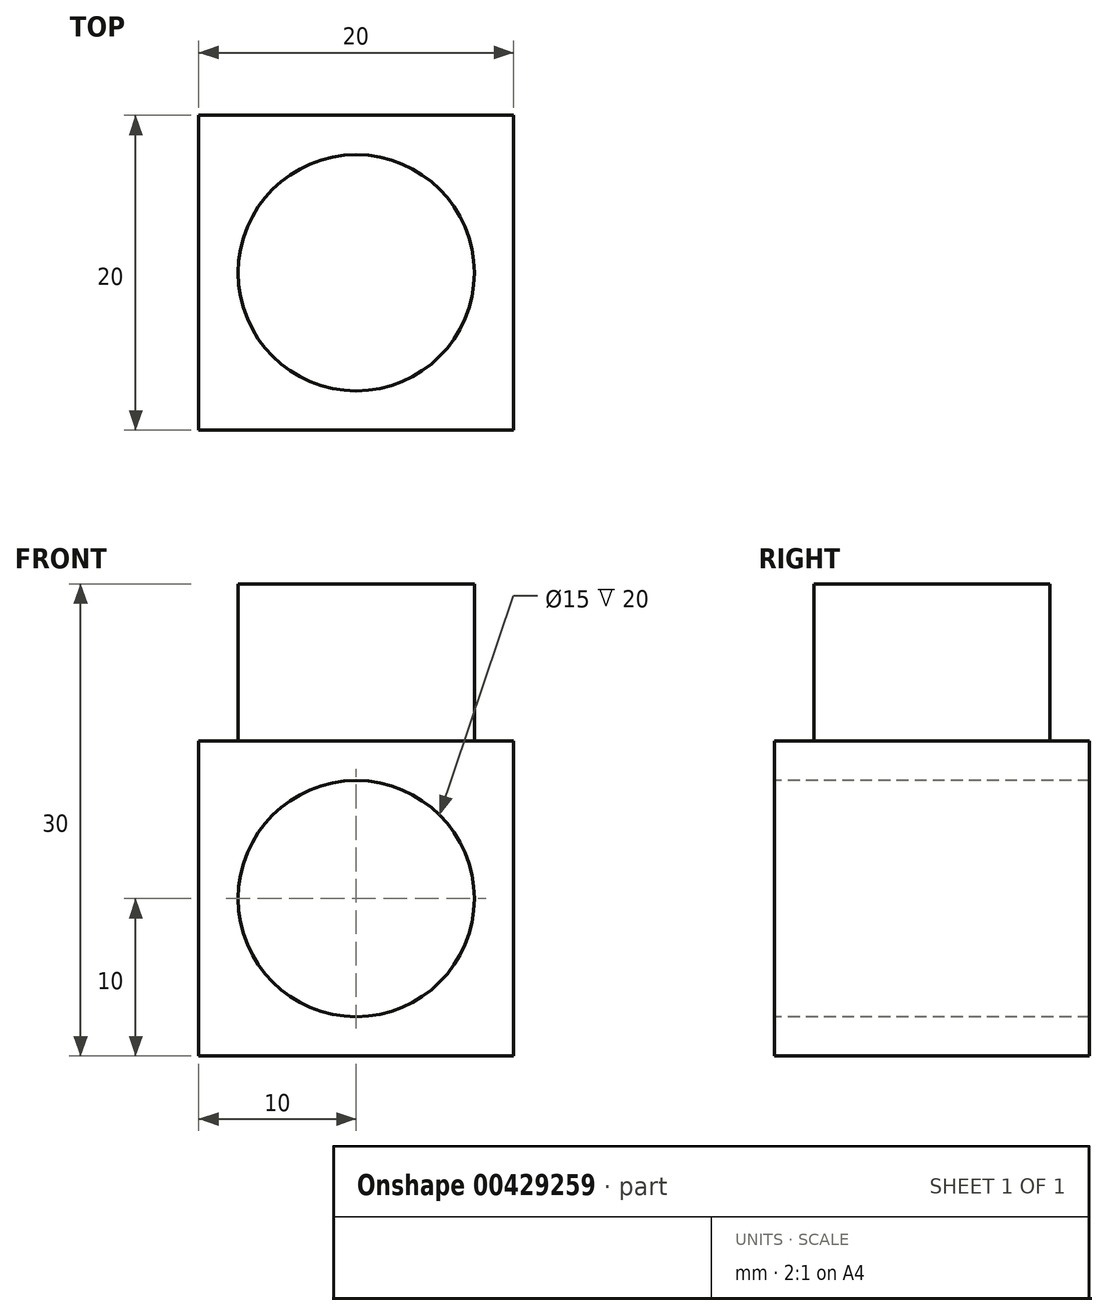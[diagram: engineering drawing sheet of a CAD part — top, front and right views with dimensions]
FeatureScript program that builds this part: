
annotation { "Feature Type Name" : "Feature", "Feature Type Description" : "" }
export const myFeature = defineFeature(function(context is Context, id is Id, definition is map)
    precondition{}
    {
        {
            var Q0;
            Q0=qCreatedBy(makeId("Front.planeOp"),FACE);
            var sketch = newSketch(context, id + "F0", { "sketchPlane" : qUnion([Q0])});
            skLineSegment(sketch, "E0.bottom", {"start": v(0, 0) * mm, "end": v(20, 0) * mm});
            skLineSegment(sketch, "E0.top", {"start": v(0, 20) * mm, "end": v(20, 20) * mm});
            skLineSegment(sketch, "E0.left", {"start": v(0, 0) * mm, "end": v(0, 20) * mm});
            skLineSegment(sketch, "E0.right", {"start": v(20, 0) * mm, "end": v(20, 20) * mm});
            skSolve(sketch);
        }
        {
            var Q0;
            Q0 = qSketchRegion(id + "F0", true);
            extrude(context, id + "F1", {"entities" : qUnion([Q0]), "depth" : 20 * mm});
        }
        {
            var Q0;
            Q0=makeQuery(id+"F1.opExtrude","SWEPT_FACE",FACE,{"disambiguationData":[OSD([sQuery(id+"F0.wireOp",EDGE,"E0.top")])]});
            var sketch = newSketch(context, id + "F2", { "sketchPlane" : qUnion([Q0])});
            skCircle(sketch, "E1", {"center": v(10, -10) * mm, "radius": 7.5 * mm});
            skPoint(sketch, "E1.centerSnap0", {"position": v(0, -10) * mm});
            skPoint(sketch, "E1.centerSnap1", {"position": v(10, 0) * mm});
            skSolve(sketch);
        }
        {
            var Q0;
            Q0 = qSketchRegion(id + "F2", true);
            extrude(context, id + "F3", {"entities" : qUnion([Q0]), "operationType" : NewBodyOperationType.ADD, "depth" : 10 * mm});
        }
        {
            var Q0;
            Q0=makeQuery(id+"F1.opExtrude","CAP_FACE",FACE,{"disambiguationData":[OSD([sQuery(id+"F0.wireOp",EDGE,"E0.bottom"),sQuery(id+"F0.wireOp",EDGE,"E0.top"),sQuery(id+"F0.wireOp",EDGE,"E0.left"),sQuery(id+"F0.wireOp",EDGE,"E0.right")])],"isStart":false});
            var sketch = newSketch(context, id + "F4", { "sketchPlane" : qUnion([Q0])});
            skCircle(sketch, "E2", {"center": v(10, 10) * mm, "radius": 7.5 * mm});
            skPoint(sketch, "E2.centerSnap0", {"position": v(0, 10) * mm});
            skPoint(sketch, "E2.centerSnap1", {"position": v(10, 20) * mm});
            skSolve(sketch);
        }
        {
            var Q0;
            Q0 = qSketchRegion(id + "F4", true);
            extrude(context, id + "F5", {"entities" : qUnion([Q0]), "operationType" : NewBodyOperationType.REMOVE, "oppositeDirection" : true, "depth" : 25 * mm});
        }
    });
